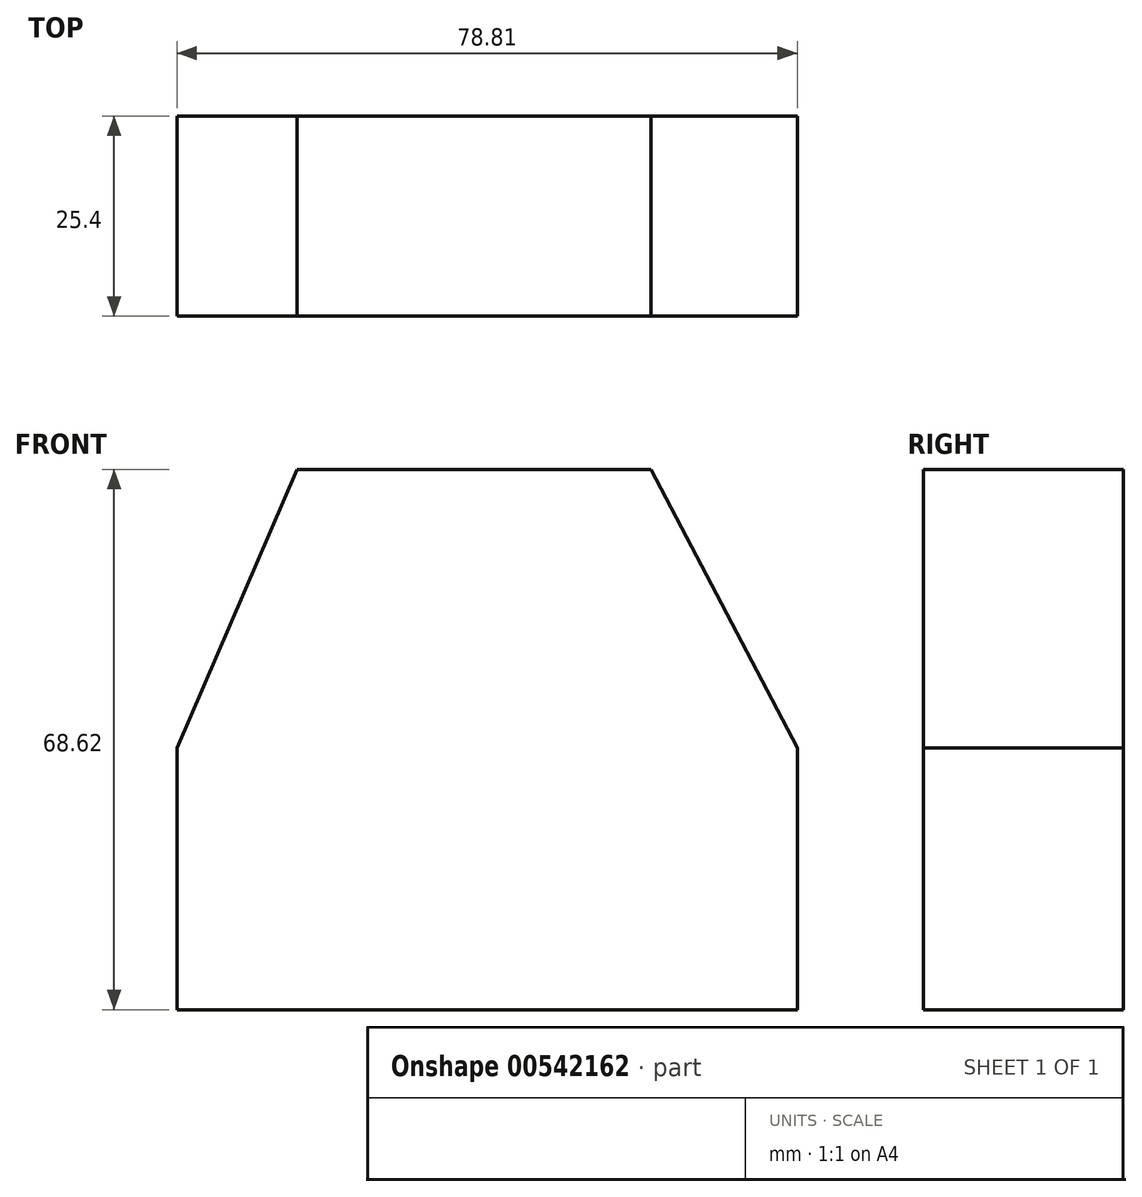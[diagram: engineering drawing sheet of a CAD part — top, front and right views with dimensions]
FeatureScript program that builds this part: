
annotation { "Feature Type Name" : "Feature", "Feature Type Description" : "" }
export const myFeature = defineFeature(function(context is Context, id is Id, definition is map)
    precondition{}
    {
        {
            var Q0;
            Q0=qCreatedBy(makeId("Front.planeOp"),FACE);
            var sketch = newSketch(context, id + "F0", { "sketchPlane" : qUnion([Q0])});
            skLineSegment(sketch, "E0", {"start": v(-21.28, 35.36) * mm, "end": v(23.67, 35.36) * mm});
            skLineSegment(sketch, "E1", {"start": v(23.67, 35.36) * mm, "end": v(42.25, 0) * mm});
            skLineSegment(sketch, "E2", {"start": v(42.25, 0) * mm, "end": v(42.25, -33.26) * mm});
            skLineSegment(sketch, "E3", {"start": v(42.25, -33.26) * mm, "end": v(0, -33.26) * mm});
            skLineSegment(sketch, "E4", {"start": v(0, -33.26) * mm, "end": v(-36.56, -33.26) * mm});
            skLineSegment(sketch, "E5", {"start": v(-36.56, -33.26) * mm, "end": v(-36.56, 0) * mm});
            skLineSegment(sketch, "E6", {"start": v(-36.56, 0) * mm, "end": v(-21.28, 35.36) * mm});
            skSolve(sketch);
        }
        {
            var Q0;
            Q0=makeQuery(id+"F0.imprint","IMPRINT",FACE,{"disambiguationData":[TD([[makeQuery(id+"F0.imprint","IMPRINT",EDGE,{"derivedFrom":sQuery(id+"F0.wireOp",EDGE,"E0")}),-1.0]])]});
            extrude(context, id + "F1", {"entities" : qUnion([Q0]), "depth" : 25.4 * mm, "offsetDistance" : 25.4 * mm});
        }
    });
